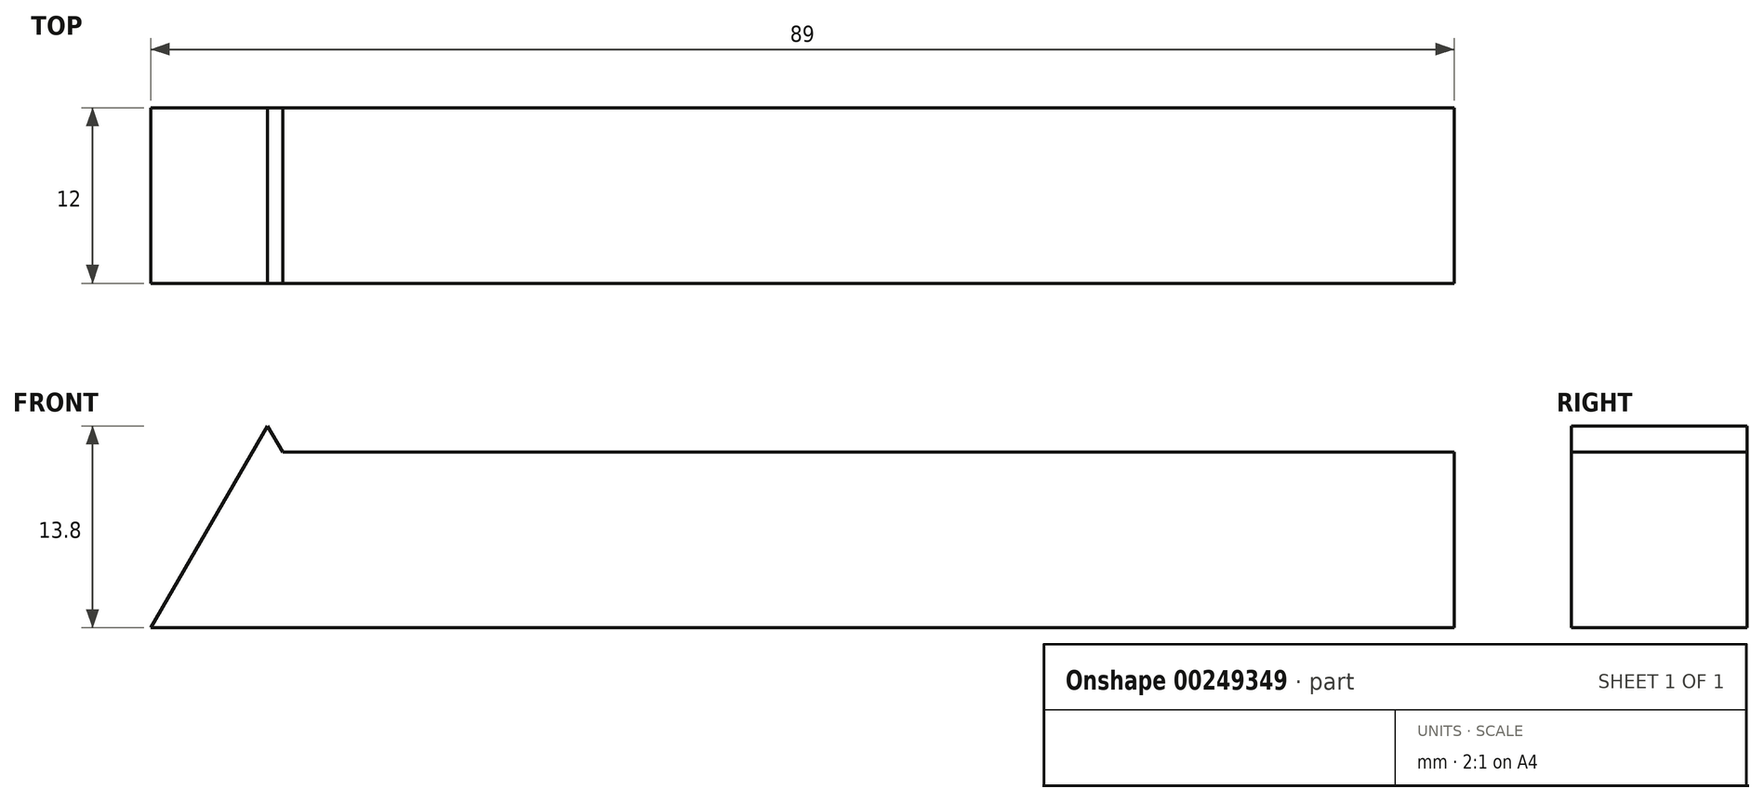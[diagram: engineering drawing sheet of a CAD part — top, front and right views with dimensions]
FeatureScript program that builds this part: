
annotation { "Feature Type Name" : "Feature", "Feature Type Description" : "" }
export const myFeature = defineFeature(function(context is Context, id is Id, definition is map)
    precondition{}
    {
        {
            var Q0;
            Q0=qCreatedBy(makeId("Front.planeOp"),FACE);
            var sketch = newSketch(context, id + "F0", { "sketchPlane" : qUnion([Q0])});
            skLineSegment(sketch, "E0", {"start": v(0, 0) * mm, "end": v(89, 0) * mm});
            skLineSegment(sketch, "E1", {"start": v(89, 0) * mm, "end": v(89, 12) * mm});
            skLineSegment(sketch, "E2", {"start": v(89, 12) * mm, "end": v(9, 12) * mm});
            skLineSegment(sketch, "E3", {"start": v(0, 0) * mm, "end": v(7.97, 13.8) * mm});
            skLineSegment(sketch, "E4", {"start": v(7.97, 13.8) * mm, "end": v(9, 12) * mm});
            skSolve(sketch);
        }
        {
            var Q0;
            Q0=makeQuery(id+"F0.imprint","IMPRINT",FACE,{"disambiguationData":[TD([[makeQuery(id+"F0.imprint","IMPRINT",EDGE,{"derivedFrom":sQuery(id+"F0.wireOp",EDGE,"cf6eb3bc-286c-4004-bd29-a7614bdbbe24.0")}),1.0]])]});
            var Q1;
            Q1=makeQuery(id+"F0.imprint","IMPRINT",FACE,{"disambiguationData":[TD([[makeQuery(id+"F0.imprint","IMPRINT",EDGE,{"derivedFrom":sQuery(id+"F0.wireOp",EDGE,"siP3TA19-M5l0-b13N-L3nD-mxQHcdo81HFG.bottom")}),-1.0]])]});
            var Q2;
            Q2=makeQuery(id+"F0.imprint","IMPRINT",FACE,{"disambiguationData":[TD([[makeQuery(id+"F0.imprint","IMPRINT",EDGE,{"derivedFrom":sQuery(id+"F0.wireOp",EDGE,"E0")}),1.0]])]});
            extrude(context, id + "F1", {"entities" : qUnion([Q0, Q1, Q2]), "oppositeDirection" : true, "depth" : 12 * mm});
        }
    });
